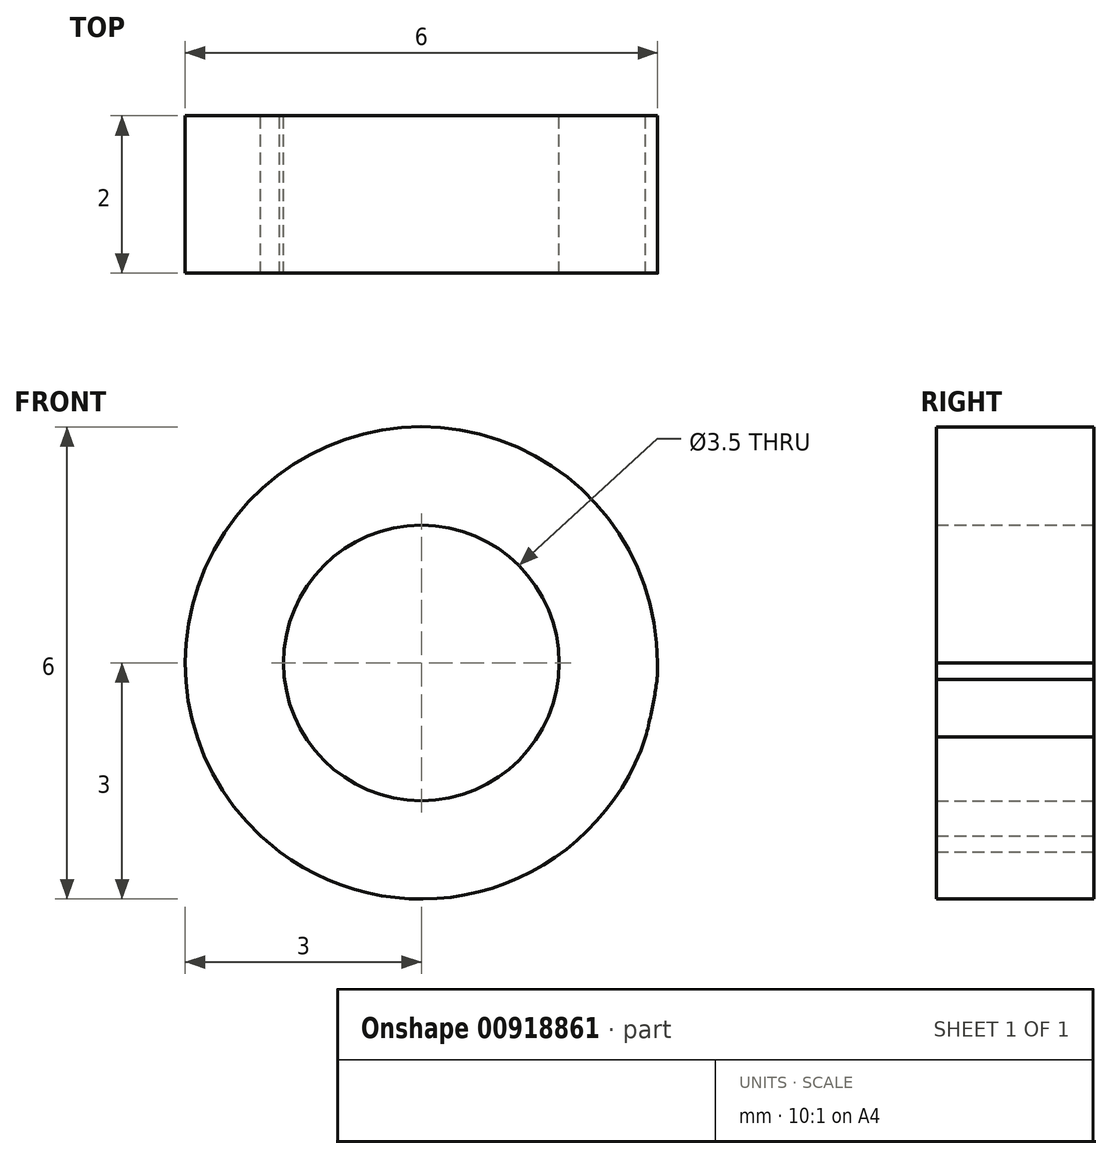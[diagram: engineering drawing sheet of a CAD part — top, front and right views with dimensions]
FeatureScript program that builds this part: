
annotation { "Feature Type Name" : "Feature", "Feature Type Description" : "" }
export const myFeature = defineFeature(function(context is Context, id is Id, definition is map)
    precondition{}
    {
        {
            var Q0;
            Q0=qCreatedBy(makeId("Front.planeOp"),FACE);
            var sketch = newSketch(context, id + "F0", { "sketchPlane" : qUnion([Q0])});
            skCircle(sketch, "E0", {"center": v(0, 0) * mm, "radius": 1.75 * mm});
            skCircle(sketch, "E1", {"center": v(0, 0) * mm, "radius": 3 * mm});
            skFitSpline(sketch, "E2", {"points": [v(-2.04, -2.2) * mm, v(-1.17, -3.97) * mm, v(-2.7, -6.08) * mm, v(-4.9, -10.6) * mm, v(-3.1, -14.86) * mm, v(5.68, -16) * mm, v(10.6, -11.56) * mm, v(3.94, -11.37) * mm, v(1.75, -6.24) * mm, v(2.29, -2.9) * mm, v(3, 0) * mm], "startDerivative": vector(50.26, -40.49) * mm, "endDerivative": vector(-1.21, 18.11) * mm});
            skSolve(sketch);
        }
        {
            var Q0;
            {var subQ0=sQuery(id+"F0.wireOp",EDGE,"E2");var subQ1=sQuery(id+"F0.wireOp",EDGE,"E1");var subQ2=makeQuery(id+"F0.imprint","INTERSECT",VERTEX,{"disambiguationData":[OD(2.0)],"derivedFrom":[subQ1,subQ0]});Q0=makeQuery(id+"F0.imprint","IMPRINT",FACE,{"disambiguationData":[TD([[makeQuery(id+"F0.imprint","IMPRINT",EDGE,{"disambiguationData":[TD([[subQ2,-1.0]])],"derivedFrom":subQ1}),-1.0]])]});}
            var Q1;
            Q1=makeQuery(id+"F0.imprint","IMPRINT",FACE,{"disambiguationData":[TD([[makeQuery(id+"F0.imprint","IMPRINT",EDGE,{"derivedFrom":sQuery(id+"F0.wireOp",EDGE,"E0")}),-1.0]])]});
            extrude(context, id + "F1", {"entities" : qUnion([Q0, Q1]), "depth" : 2 * mm, "offsetDistance" : 25 * mm});
        }
    });
